# Revit family: PTPS-1000
name_source: partatom
category: Mechanical Equipment
units: mm (PartAtom-declared; Revit-internal decimal feet)

## family parameters
Always vertical = Yes
Cut with Voids When Loaded = No
OmniClass Number = 23.75.00.00
OmniClass Title = Climate Control (HVAC)
Part Type = Normal
Room Calculation Point = No
Round Connector Dimension = Use Diameter
Shared = No
Work Plane-Based = No

## types (1)
- PTPS-1000
    Default Elevation = 0 mm  [stored 0 ft]
    Dia = 900 mm  [stored 2.95276 ft]
    Footing = 17 mm
    H1 = 345 mm  [stored 1.13189 ft]
    H2 = 427 mm  [stored 1.40092 ft]
    H3 = 405 mm
    H4 = 465 mm  [stored 1.52559 ft]
    H5 = 565 mm  [stored 1.85367 ft]
    H6 = 965 mm  [stored 3.16601 ft]
    H7 = 1405 mm  [stored 4.60958 ft]
    H8 = 1725 mm  [stored 5.65945 ft]
    H9 = 1925 mm  [stored 6.31562 ft]
    Height = 2250 mm
    Max CWE Valve Setting = 800.0 kPa
    Max Supply Pressure = 600.0 kPa
    Max TPR Valve Setting = 1000.0 kPa

note: [stored X ft] marks values corroborated as IEEE doubles in the binary element streams (Revit-internal decimal feet)

## geometry (parser evidence)
native form markers: Sweep x2
no freeform markers — native parametric forms only
